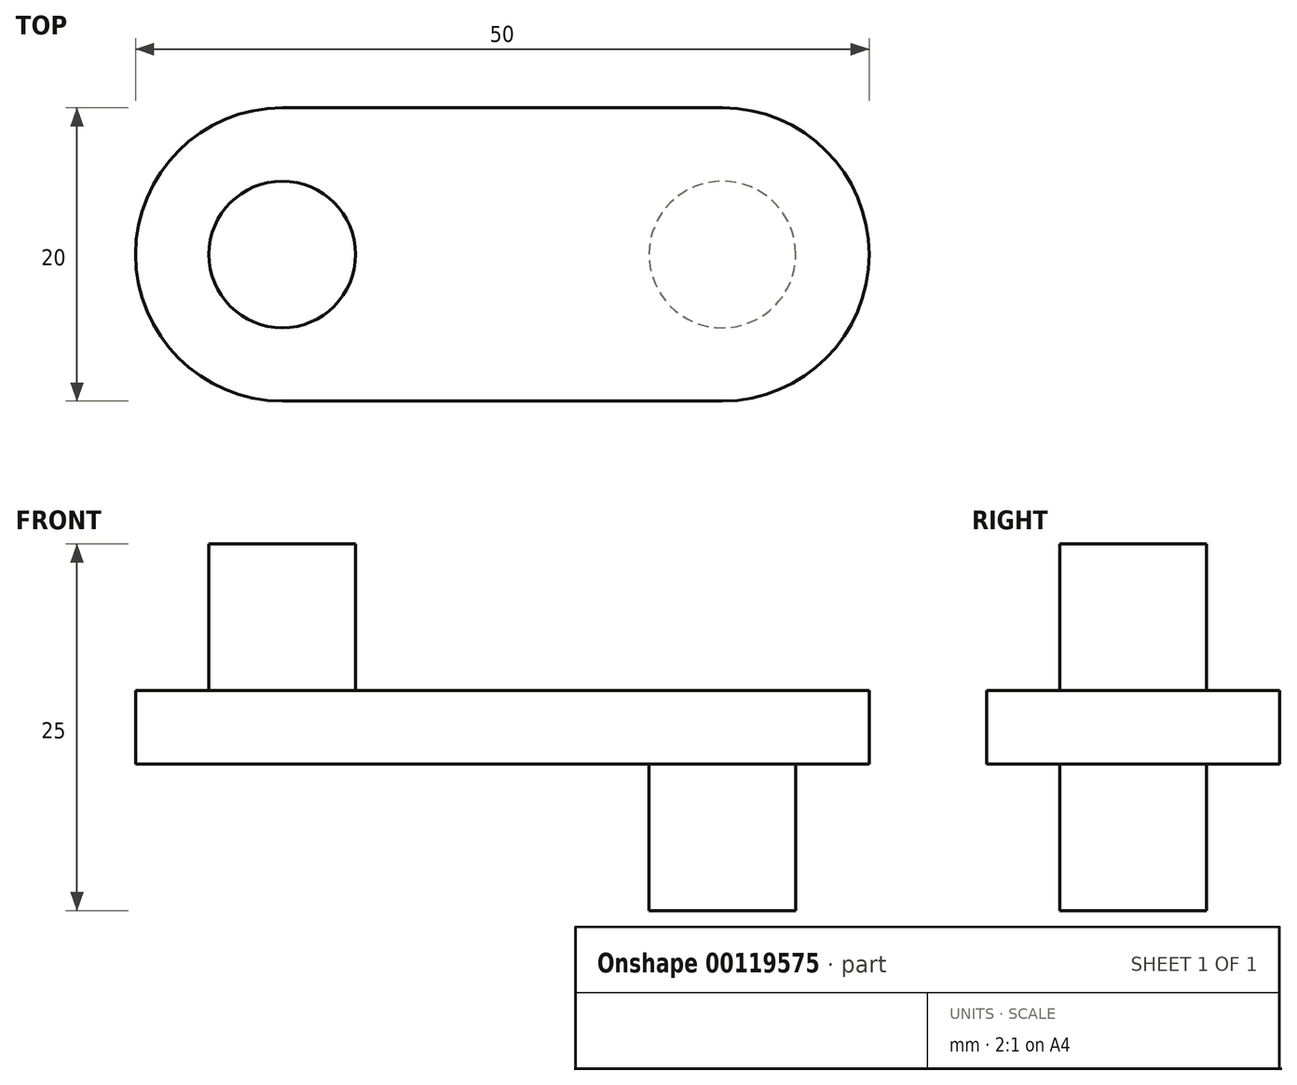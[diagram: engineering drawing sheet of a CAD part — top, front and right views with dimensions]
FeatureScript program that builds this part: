
annotation { "Feature Type Name" : "Feature", "Feature Type Description" : "" }
export const myFeature = defineFeature(function(context is Context, id is Id, definition is map)
    precondition{}
    {
        {
            var Q0;
            Q0=qCreatedBy(makeId("Top.planeOp"),FACE);
            var sketch = newSketch(context, id + "F0", { "sketchPlane" : qUnion([Q0])});
            skLineSegment(sketch, "E0.bottom", {"start": v(0, 0) * mm, "end": v(-30, 0) * mm});
            skLineSegment(sketch, "E0.top", {"start": v(0, -20) * mm, "end": v(-30, -20) * mm});
            skArc(sketch, "E1", {"start": v(-30, 0) * mm, "mid": v(-40, -10) * mm, "end": v(-30, -20) * mm});
            skArc(sketch, "E2", {"start": v(0, 0) * mm, "mid": v(10, -10) * mm, "end": v(0, -20) * mm});
            skSolve(sketch);
        }
        {
            var Q0;
            Q0 = qSketchRegion(id + "F0", true);
            extrude(context, id + "F1", {"entities" : qUnion([Q0]), "depth" : 5 * mm});
        }
        {
            var Q0;
            Q0=qCreatedBy(makeId("Top.planeOp"),FACE);
            var sketch = newSketch(context, id + "F2", { "sketchPlane" : qUnion([Q0])});
            skLineSegment(sketch, "E3", {"start": v(0, 0) * mm, "end": v(0, -10) * mm, "construction": true});
            skCircle(sketch, "E4", {"center": v(0, -10) * mm, "radius": 5 * mm});
            skSolve(sketch);
        }
        {
            var Q0;
            Q0 = qSketchRegion(id + "F2", true);
            extrude(context, id + "F3", {"entities" : qUnion([Q0]), "operationType" : NewBodyOperationType.ADD, "oppositeDirection" : true, "depth" : 10 * mm});
        }
        {
            var Q0;
            Q0=makeQuery(id+"F1.opExtrude","CAP_FACE",FACE,{"disambiguationData":[OSD([sQuery(id+"F0.wireOp",EDGE,"E0.bottom"),sQuery(id+"F0.wireOp",EDGE,"E0.top"),sQuery(id+"F0.wireOp",EDGE,"E1"),sQuery(id+"F0.wireOp",EDGE,"E2")])],"isStart":false});
            var sketch = newSketch(context, id + "F4", { "sketchPlane" : qUnion([Q0])});
            skLineSegment(sketch, "E5", {"start": v(0, 0) * mm, "end": v(-30, 0) * mm, "construction": true});
            skLineSegment(sketch, "E6", {"start": v(-30, 0) * mm, "end": v(-30, -10) * mm, "construction": true});
            skCircle(sketch, "E7", {"center": v(-30, -10) * mm, "radius": 5 * mm});
            skSolve(sketch);
        }
        {
            var Q0;
            Q0 = qSketchRegion(id + "F4", true);
            extrude(context, id + "F5", {"entities" : qUnion([Q0]), "operationType" : NewBodyOperationType.ADD, "depth" : 10 * mm});
        }
    });
